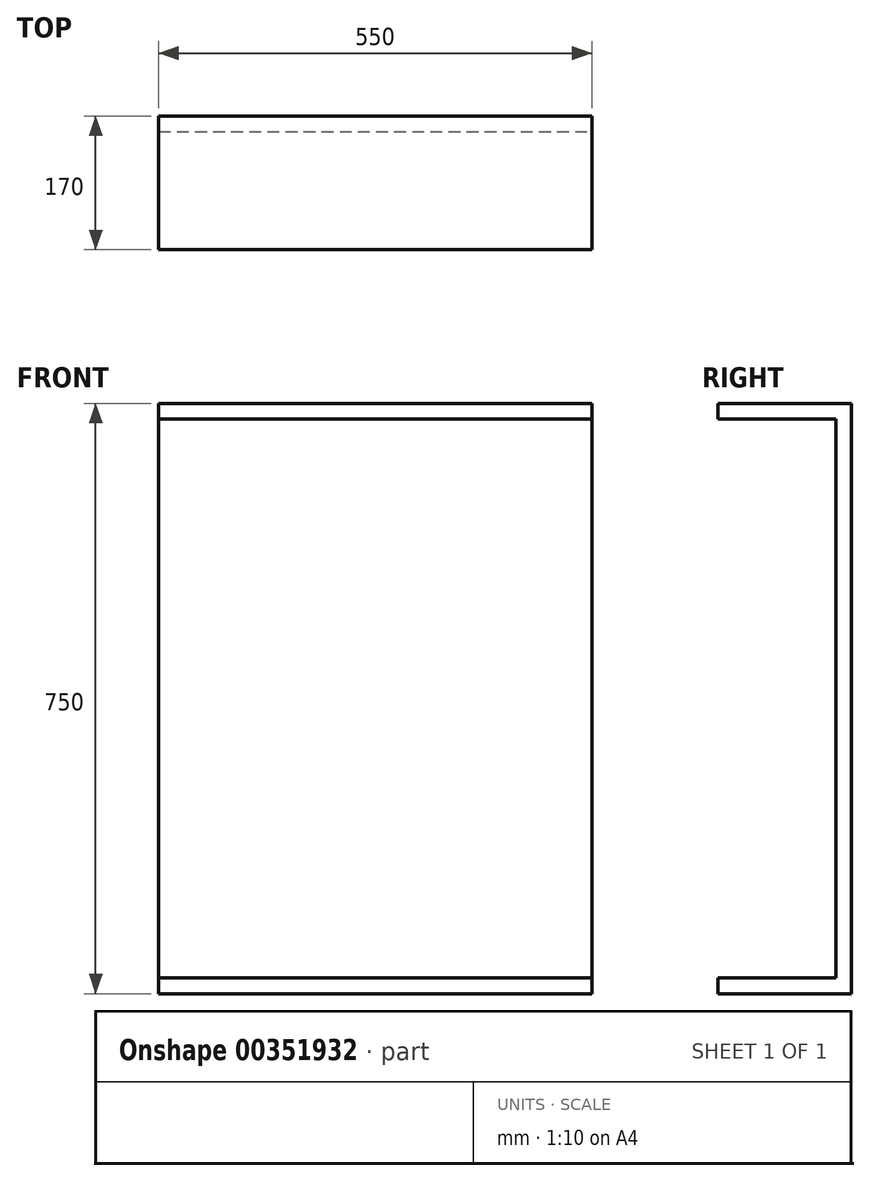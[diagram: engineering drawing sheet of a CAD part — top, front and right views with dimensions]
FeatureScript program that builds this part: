
annotation { "Feature Type Name" : "Feature", "Feature Type Description" : "" }
export const myFeature = defineFeature(function(context is Context, id is Id, definition is map)
    precondition{}
    {
        {
            var Q0;
            Q0=qCreatedBy(makeId("Top.planeOp"),FACE);
            var sketch = newSketch(context, id + "F0", { "sketchPlane" : qUnion([Q0])});
            skLineSegment(sketch, "E0.bottom", {"start": v(-279.85, 89.63) * mm, "end": v(270.15, 89.63) * mm});
            skLineSegment(sketch, "E0.top", {"start": v(-279.85, -80.37) * mm, "end": v(270.15, -80.37) * mm});
            skLineSegment(sketch, "E0.left", {"start": v(-279.85, 89.63) * mm, "end": v(-279.85, -80.37) * mm});
            skLineSegment(sketch, "E0.right", {"start": v(270.15, 89.63) * mm, "end": v(270.15, -80.37) * mm});
            skSolve(sketch);
        }
        {
            var Q0;
            Q0=makeQuery(id+"F0.imprint","IMPRINT",FACE,{"disambiguationData":[TD([[makeQuery(id+"F0.imprint","IMPRINT",EDGE,{"derivedFrom":sQuery(id+"F0.wireOp",EDGE,"E0.bottom")}),-1.0]])]});
            extrude(context, id + "F1", {"entities" : qUnion([Q0]), "depth" : 750 * mm});
        }
        {
            var Q0;
            Q0=makeQuery(id+"F1.opExtrude","SWEPT_FACE",FACE,{"disambiguationData":[OSD([sQuery(id+"F0.wireOp",EDGE,"E0.top")])]});
            var sketch = newSketch(context, id + "F2", { "sketchPlane" : qUnion([Q0])});
            skLineSegment(sketch, "E1", {"start": v(-279.85, 730) * mm, "end": v(270.15, 730) * mm});
            skLineSegment(sketch, "E2", {"start": v(-279.85, 20) * mm, "end": v(270.15, 20) * mm});
            skLineSegment(sketch, "E3", {"start": v(-279.85, 730) * mm, "end": v(-279.85, 20) * mm});
            skLineSegment(sketch, "E4", {"start": v(270.15, 730) * mm, "end": v(270.15, 20) * mm});
            skSolve(sketch);
        }
        {
            var Q0;
            Q0=makeQuery(id+"F2.imprint","IMPRINT",FACE,{"disambiguationData":[TD([[makeQuery(id+"F2.imprint","IMPRINT",EDGE,{"derivedFrom":sQuery(id+"F2.wireOp",EDGE,"E1")}),-1.0]])]});
            extrude(context, id + "F3", {"entities" : qUnion([Q0]), "operationType" : NewBodyOperationType.REMOVE, "oppositeDirection" : true, "depth" : 150 * mm});
        }
    });
